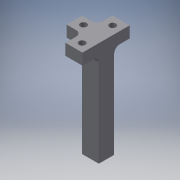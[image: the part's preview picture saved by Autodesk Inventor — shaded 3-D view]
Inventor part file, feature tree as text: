
AUTODESK INVENTOR PART (.ipt)
format: ipt  version: 2018 (Build 220112000, 112)  size: 178,688 bytes
history: native  units: mm
features: sketch x5, other x3
ambient origin geometry x8: Origin, YZ Plane, XZ Plane, XY Plane, X Axis, Y Axis, Z Axis, Center Point
bodies: Volumenkörper1 (feature_tree)
feature tree (8):
  other  "SolarpanelHalterung1.ipt"
  other  "Volumenkörper1::SolarpanelHalterung1.ipt"
  other  "Bezeichnung1"
  sketch  "Skizze1"  dims[d0=10.0mm]
  sketch  "Skizze2"
  sketch  "Skizze3"
  sketch  "Skizze4"
  sketch  "Skizze5"
